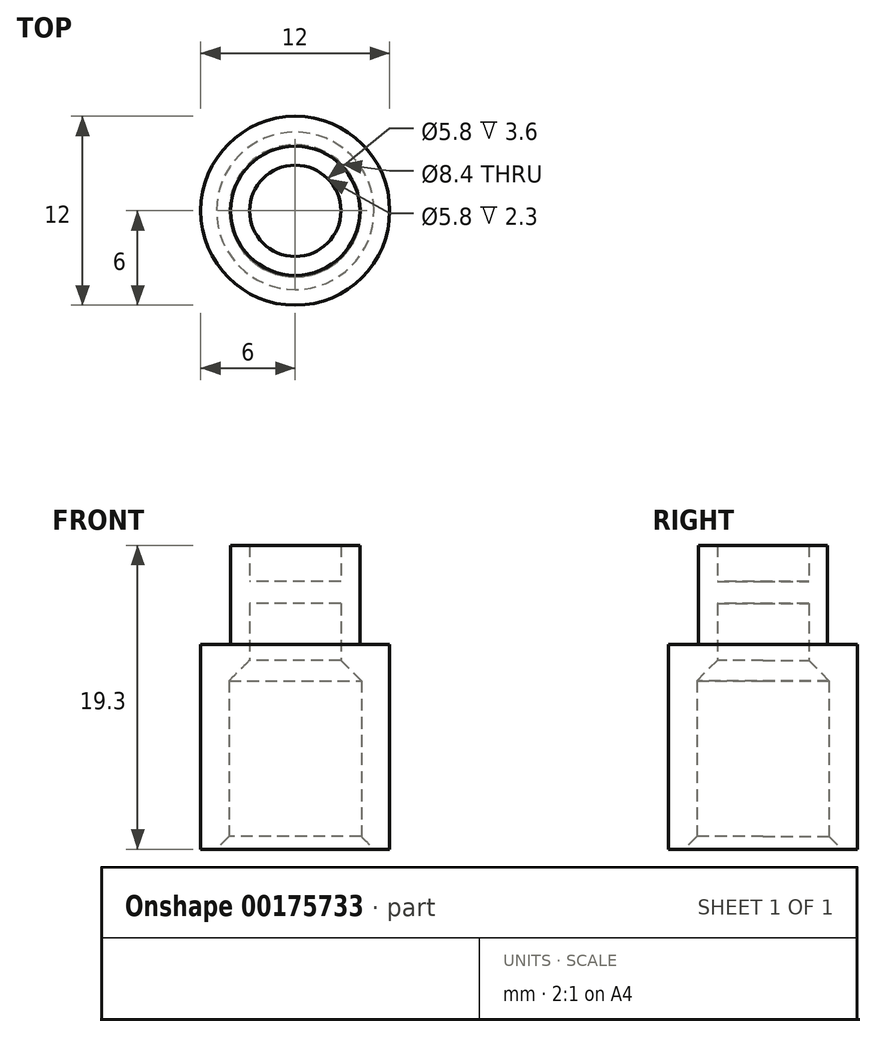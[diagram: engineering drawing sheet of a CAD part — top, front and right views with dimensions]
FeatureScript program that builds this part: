
annotation { "Feature Type Name" : "Feature", "Feature Type Description" : "" }
export const myFeature = defineFeature(function(context is Context, id is Id, definition is map)
    precondition{}
    {
        {
            var Q0;
            Q0=qCreatedBy(makeId("Top.planeOp"),FACE);
            var sketch = newSketch(context, id + "F0", { "sketchPlane" : qUnion([Q0])});
            skCircle(sketch, "E0", {"center": v(0, 0) * mm, "radius": 6 * mm});
            skCircle(sketch, "E1", {"center": v(0, 0) * mm, "radius": 4.2 * mm});
            skSolve(sketch);
        }
        {
            var Q0;
            Q0 = qSketchRegion(id + "F0", true);
            extrude(context, id + "F1", {"entities" : qUnion([Q0]), "depth" : 13 * mm});
        }
        {
            var Q0;
            Q0=makeQuery(id+"F1.opExtrude","CAP_FACE",FACE,{"disambiguationData":[OSD([sQuery(id+"F0.wireOp",EDGE,"E0"),sQuery(id+"F0.wireOp",EDGE,"E1")])],"isStart":false});
            var sketch = newSketch(context, id + "F2", { "sketchPlane" : qUnion([Q0])});
            skCircle(sketch, "E2", {"center": v(0, 0) * mm, "radius": 4.1 * mm});
            skCircle(sketch, "E3", {"center": v(0, 0) * mm, "radius": 2.9 * mm});
            skSolve(sketch);
        }
        {
            var Q0;
            Q0 = qSketchRegion(id + "F2", true);
            extrude(context, id + "F3", {"entities" : qUnion([Q0]), "depth" : 6.3 * mm});
        }
        {
            var Q0;
            Q0=makeQuery(id+"F1.opExtrude","CAP_FACE",FACE,{"disambiguationData":[OSD([sQuery(id+"F0.wireOp",EDGE,"E0"),sQuery(id+"F0.wireOp",EDGE,"E1")])],"isStart":false});
            var sketch = newSketch(context, id + "F4", { "sketchPlane" : qUnion([Q0])});
            skCircle(sketch, "E4", {"center": v(0, 0) * mm, "radius": 4.2 * mm});
            skCircle(sketch, "E5", {"center": v(0, 0) * mm, "radius": 2.9 * mm});
            skSolve(sketch);
        }
        {
            var Q0;
            Q0 = qSketchRegion(id + "F4", true);
            extrude(context, id + "F5", {"entities" : qUnion([Q0]), "operationType" : NewBodyOperationType.ADD, "oppositeDirection" : true, "depth" : 3 * mm});
        }
        {
            var Q0;
            Q0=makeQuery(id+"F5.opExtrude","CAP_EDGE",EDGE,{"disambiguationData":[OSD([sQuery(id+"F4.wireOp",EDGE,"E5")])],"isStart":false});
            chamfer(context, id + "F6", {"entities" : qUnion([Q0]), "width" : 2 * mm, "tangentPropagation" : true});
        }
        {
            var Q0;
            Q0=makeQuery(id+"F1.opExtrude","CAP_EDGE",EDGE,{"disambiguationData":[OSD([sQuery(id+"F0.wireOp",EDGE,"E1")])],"isStart":true});
            chamfer(context, id + "F7", {"entities" : qUnion([Q0]), "width" : 0.8 * mm, "tangentPropagation" : true});
        }
        {
            var Q0;
            Q0=makeQuery(id+"F3.opExtrude","CAP_FACE",FACE,{"disambiguationData":[OSD([sQuery(id+"F2.wireOp",EDGE,"E2"),sQuery(id+"F2.wireOp",EDGE,"E3")])],"isStart":false});
            cPlane(context, id + "F8", {"entities" : qUnion([Q0]), "cplaneType" : CPlaneType.OFFSET, "offset" : 3 * mm, "oppositeDirection" : true, "width" : 150 * mm, "height" : 150 * mm});
        }
        {
            var Q0;
            Q0=qCreatedBy(id+"F8.planeOp",FACE);
            var sketch = newSketch(context, id + "F9", { "sketchPlane" : qUnion([Q0])});
            skCircle(sketch, "E6", {"center": v(0, 0) * mm, "radius": 4.1 * mm});
            skSolve(sketch);
        }
        {
            var Q0;
            Q0 = qSketchRegion(id + "F9", true);
            extrude(context, id + "F10", {"entities" : qUnion([Q0]), "operationType" : NewBodyOperationType.ADD, "endBound" : BoundingType.SYMMETRIC, "depth" : 1.4 * mm});
        }
    });
